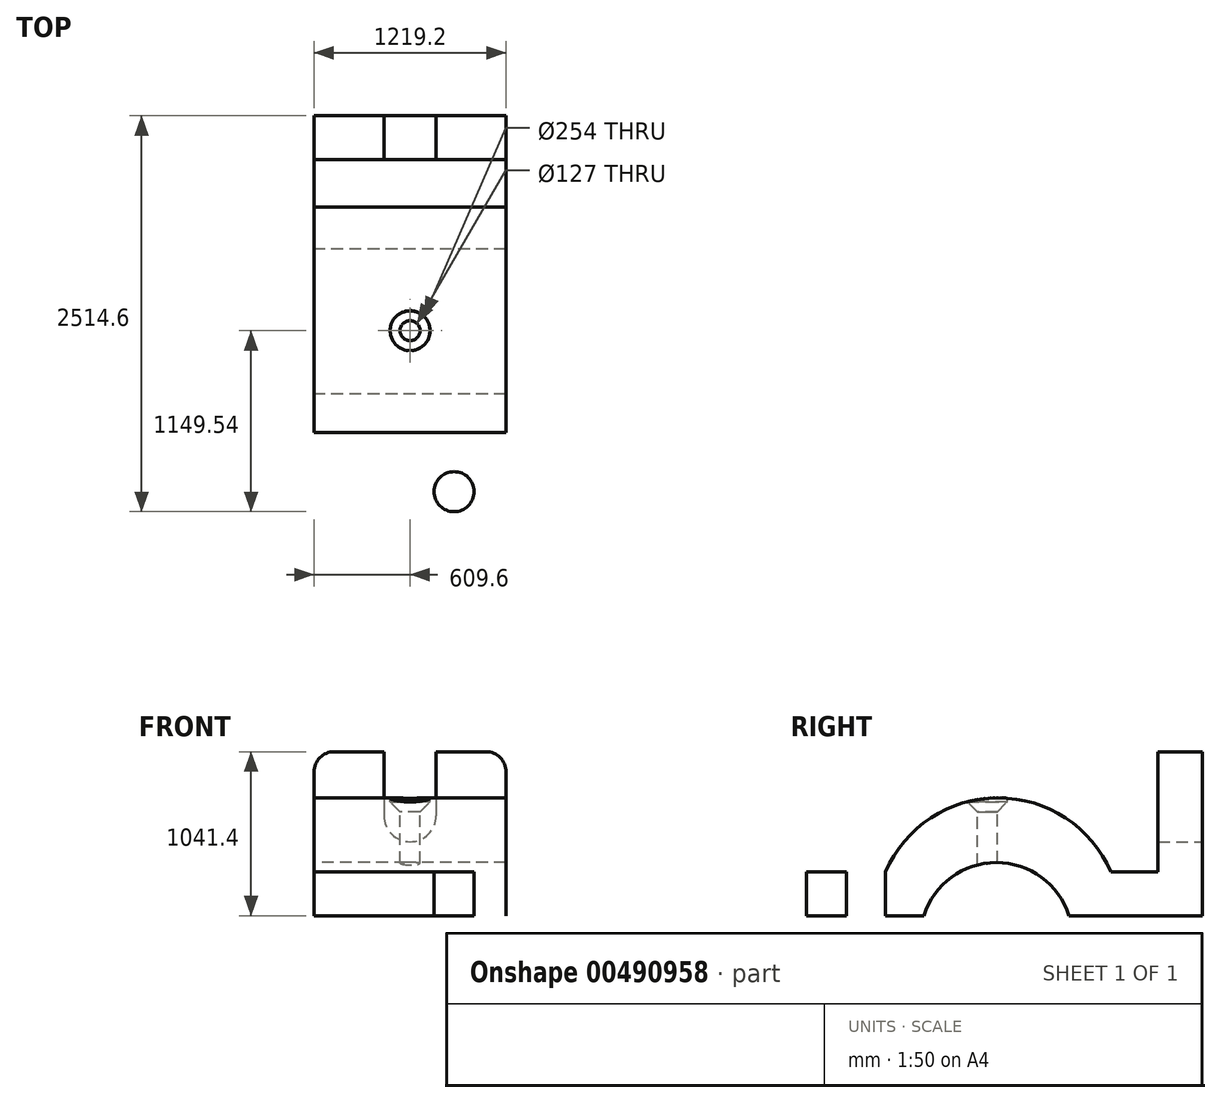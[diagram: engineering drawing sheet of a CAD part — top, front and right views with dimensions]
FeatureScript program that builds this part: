
annotation { "Feature Type Name" : "Feature", "Feature Type Description" : "" }
export const myFeature = defineFeature(function(context is Context, id is Id, definition is map)
    precondition{}
    {
        {
            var Q0;
            Q0=qCreatedBy(makeId("Right.planeOp"),FACE);
            var sketch = newSketch(context, id + "F0", { "sketchPlane" : qUnion([Q0])});
            skLineSegment(sketch, "E0", {"start": v(1144.4, 0) * mm, "end": v(1144.4, 1041.4) * mm});
            skLineSegment(sketch, "E1", {"start": v(1144.4, 1041.4) * mm, "end": v(865, 1041.4) * mm});
            skLineSegment(sketch, "E2", {"start": v(865, 1041.4) * mm, "end": v(865, 279.4) * mm});
            skLineSegment(sketch, "E3", {"start": v(865, 279.4) * mm, "end": v(565.05, 279.4) * mm});
            skLineSegment(sketch, "E4", {"start": v(-867.04, 279.4) * mm, "end": v(-1573.4, 279.4) * mm});
            skLineSegment(sketch, "E5", {"start": v(-1573.4, 279.4) * mm, "end": v(-1573.4, 0) * mm});
            skLineSegment(sketch, "E6", {"start": v(-1573.4, 0) * mm, "end": v(-867.04, 0) * mm});
            skLineSegment(sketch, "E7", {"start": v(565.05, 0) * mm, "end": v(1144.4, 0) * mm});
            skLineSegment(sketch, "E8", {"start": v(-867.04, 0) * mm, "end": v(-622.56, 0) * mm});
            skLineSegment(sketch, "E9", {"start": v(565.05, 0) * mm, "end": v(297.81, 0) * mm});
            skArc(sketch, "E10", {"start": v(297.81, 0) * mm, "mid": v(-162.37, 337.23) * mm, "end": v(-622.56, 0) * mm});
            skArc(sketch, "E11", {"start": v(565.05, 279.4) * mm, "mid": v(-151, 748.38) * mm, "end": v(-867.04, 279.4) * mm});
            skSolve(sketch);
        }
        {
            var Q0;
            Q0=qSketchRegion(id+"F0",true);
            extrude(context, id + "F1", {"entities" : qUnion([Q0]), "depth" : 609.6 * mm, "hasSecondDirection" : true, "secondDirectionOppositeDirection" : true, "secondDirectionDepth" : 609.6 * mm});
        }
        {
            var Q0;
            Q0=makeQuery(id+"F1.opExtrude","SWEPT_FACE",FACE,{"disambiguationData":[OSD([sQuery(id+"F0.wireOp",EDGE,"E4")])]});
            var sketch = newSketch(context, id + "F2", { "sketchPlane" : qUnion([Q0])});
            skCircle(sketch, "E12", {"center": v(-279.4, -1243.2) * mm, "radius": 127 * mm});
            skLineSegment(sketch, "E13", {"start": v(0, -867.04) * mm, "end": v(0, -1573.4) * mm, "construction": true});
            skCircle(sketch, "E14.MirrorC", {"center": v(279.4, -1243.2) * mm, "radius": 127 * mm});
            skSolve(sketch);
        }
        {
            var Q0;
            Q0=makeQuery(id+"F1.opExtrude","SWEPT_FACE",FACE,{"disambiguationData":[OSD([sQuery(id+"F0.wireOp",EDGE,"E0")])]});
            var sketch = newSketch(context, id + "F3", { "sketchPlane" : qUnion([Q0])});
            skLineSegment(sketch, "E15", {"start": v(-609.6, 1041.4) * mm, "end": v(-165.1, 1041.4) * mm});
            skLineSegment(sketch, "E16", {"start": v(609.6, 1041.4) * mm, "end": v(165.1, 1041.4) * mm});
            skLineSegment(sketch, "E17", {"start": v(-165.1, 1041.4) * mm, "end": v(-165.1, 635) * mm});
            skLineSegment(sketch, "E18", {"start": v(165.1, 1041.4) * mm, "end": v(165.1, 635) * mm});
            skArc(sketch, "E19", {"start": v(-165.1, 635) * mm, "mid": v(0, 469.9) * mm, "end": v(165.1, 635) * mm});
            skSolve(sketch);
        }
        {
            var Q0;
            {var subQ0=sQuery(id+"F3.wireOp",EDGE,"E17");Q0=makeQuery(id+"F3.imprint","IMPRINT",FACE,{"disambiguationData":[TD([[makeQuery(id+"F3.imprint","IMPRINT",EDGE,{"derivedFrom":subQ0}),1.0]])]});}
            extrude(context, id + "F4", {"entities" : qUnion([Q0]), "operationType" : NewBodyOperationType.REMOVE, "oppositeDirection" : true, "depth" : 452.12 * mm});
        }
        {
            var Q0;
            Q0=makeQuery(id+"F1.opExtrude","CAP_EDGE",EDGE,{"disambiguationData":[OSD([sQuery(id+"F0.wireOp",EDGE,"E1")])],"isStart":false});
            var Q1;
            Q1=makeQuery(id+"F1.opExtrude","CAP_EDGE",EDGE,{"disambiguationData":[OSD([sQuery(id+"F0.wireOp",EDGE,"E1")])],"isStart":true});
            fillet(context, id + "F5", {"entities" : qUnion([Q0, Q1]), "radius" : 127 * mm, "tangentPropagation" : true, "allowEdgeOverflow" : false});
        }
        {
            var Q0;
            Q0=makeQuery(id+"F1.opExtrude","CAP_EDGE",EDGE,{"disambiguationData":[OSD([sQuery(id+"F0.wireOp",EDGE,"E5")])],"isStart":true});
            var Q1;
            Q1=makeQuery(id+"F1.opExtrude","CAP_EDGE",EDGE,{"disambiguationData":[OSD([sQuery(id+"F0.wireOp",EDGE,"E5")])],"isStart":false});
            fillet(context, id + "F6", {"entities" : qUnion([Q0, Q1]), "radius" : 330.2 * mm, "tangentPropagation" : true, "allowEdgeOverflow" : false});
        }
        {
            var Q0;
            Q0=makeQuery(id+"F2.imprint","IMPRINT",FACE,{"disambiguationData":[TD([[makeQuery(id+"F2.imprint","IMPRINT",EDGE,{"derivedFrom":sQuery(id+"F2.wireOp",EDGE,"E12")}),1.0]])]});
            var Q1;
            Q1=makeQuery(id+"F2.imprint","IMPRINT",FACE,{"disambiguationData":[TD([[makeQuery(id+"F2.imprint","IMPRINT",EDGE,{"derivedFrom":sQuery(id+"F2.wireOp",EDGE,"E14.MirrorC")}),-1.0]])]});
            extrude(context, id + "F7", {"entities" : qUnion([Q0, Q1]), "operationType" : NewBodyOperationType.REMOVE, "oppositeDirection" : true, "depth" : 665.48 * mm});
        }
        {
            var Q0;
            Q0=makeQuery(id+"F1.opExtrude","CAP_EDGE",EDGE,{"disambiguationData":[OSD([sQuery(id+"F0.wireOp",EDGE,"E11")])],"isStart":true});
            cPoint(context, id + "F8", {"entities" : qUnion([Q0]), "parameter" : 0.5});
        }
        {
            var Q0;
            Q0=qCreatedBy(makeId("Top.planeOp"),FACE);
            var Q1;
            Q1=qCreatedBy(id+"F8",VERTEX);
            cPlane(context, id + "F9", {"entities" : qUnion([Q0, Q1]), "cplaneType" : CPlaneType.PLANE_POINT, "offset" : 25.4 * mm, "width" : 152.4 * mm, "height" : 152.4 * mm});
        }
        {
            var Q0;
            Q0=qCreatedBy(id+"F9.planeOp",FACE);
            var sketch = newSketch(context, id + "F10", { "sketchPlane" : qUnion([Q0])});
            skPoint(sketch, "E20", {"position": v(0, -220.66) * mm});
            skSolve(sketch);
        }
        {
            var Q0;
            Q0=sQuery(id+"F10.wireOp",VERTEX,"E20");
            var Q1;
            Q1=makeQuery(id+"F1.opExtrude","SWEPT_BODY",BODY,{"disambiguationData":[OSD([sQuery(id+"F0.wireOp",EDGE,"E0"),sQuery(id+"F0.wireOp",EDGE,"E1"),sQuery(id+"F0.wireOp",EDGE,"E2"),sQuery(id+"F0.wireOp",EDGE,"E3"),sQuery(id+"F0.wireOp",EDGE,"E4"),sQuery(id+"F0.wireOp",EDGE,"E5"),sQuery(id+"F0.wireOp",EDGE,"E6"),sQuery(id+"F0.wireOp",EDGE,"E7"),sQuery(id+"F0.wireOp",EDGE,"E8"),sQuery(id+"F0.wireOp",EDGE,"E9"),sQuery(id+"F0.wireOp",EDGE,"E10"),sQuery(id+"F0.wireOp",EDGE,"E11")])]});
            hole(context, id + "F11", {"style" : HoleStyle.C_SINK, "endStyle" : HoleEndStyle.THROUGH, "holeDiameter" : 127 * mm, "cSinkDiameter" : 254 * mm, "cSinkAngle" : 90 * degree, "locations" : qUnion([Q0]), "scope" : qUnion([Q1]), "isTappedThrough" : true});
        }
    });
